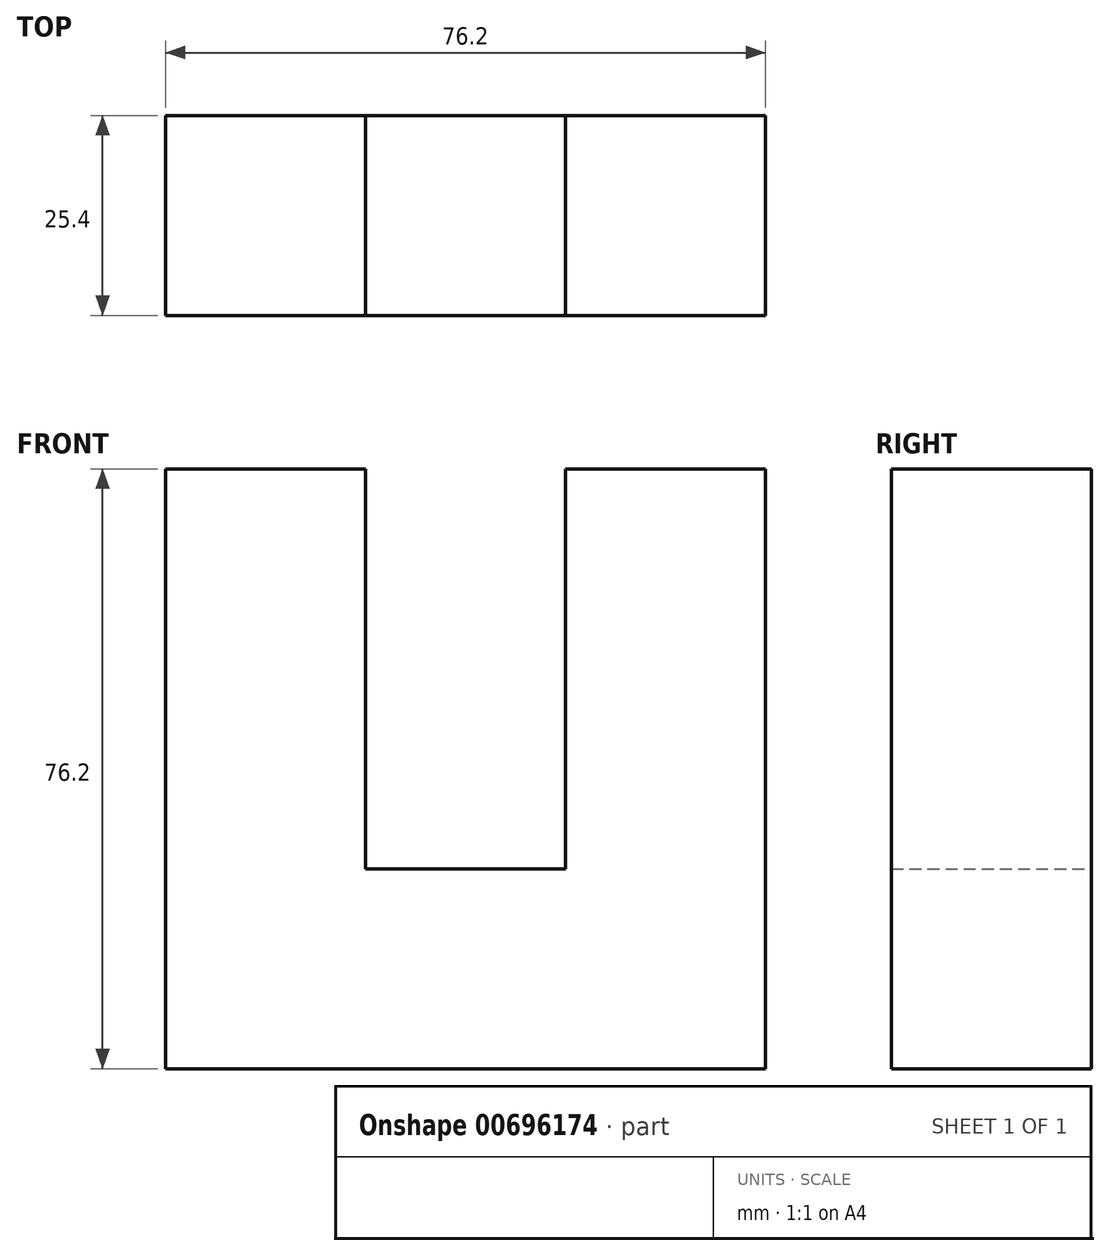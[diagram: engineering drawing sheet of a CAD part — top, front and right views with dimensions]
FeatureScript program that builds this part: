
annotation { "Feature Type Name" : "Feature", "Feature Type Description" : "" }
export const myFeature = defineFeature(function(context is Context, id is Id, definition is map)
    precondition{}
    {
        {
            var Q0;
            Q0=qCreatedBy(makeId("Front.planeOp"),FACE);
            var sketch = newSketch(context, id + "F0", { "sketchPlane" : qUnion([Q0])});
            skLineSegment(sketch, "E0", {"start": v(-25.4, 48.41) * mm, "end": v(-25.4, -27.79) * mm});
            skLineSegment(sketch, "E1", {"start": v(-25.4, -27.79) * mm, "end": v(50.8, -27.79) * mm});
            skLineSegment(sketch, "E2", {"start": v(50.8, -27.79) * mm, "end": v(50.8, 48.41) * mm});
            skLineSegment(sketch, "E3", {"start": v(50.8, 48.41) * mm, "end": v(25.4, 48.41) * mm});
            skLineSegment(sketch, "E4", {"start": v(25.4, 48.41) * mm, "end": v(25.4, -2.39) * mm});
            skLineSegment(sketch, "E5", {"start": v(25.4, -2.39) * mm, "end": v(0, -2.39) * mm});
            skLineSegment(sketch, "E6", {"start": v(0, -2.39) * mm, "end": v(0, 48.41) * mm});
            skLineSegment(sketch, "E7", {"start": v(-25.4, 48.41) * mm, "end": v(0, 48.41) * mm});
            skSolve(sketch);
        }
        {
            var Q0;
            Q0=makeQuery(id+"F0.imprint","IMPRINT",FACE,{"disambiguationData":[TD([[makeQuery(id+"F0.imprint","IMPRINT",EDGE,{"derivedFrom":sQuery(id+"F0.wireOp",EDGE,"E0")}),1.0]])]});
            extrude(context, id + "F1", {"entities" : qUnion([Q0]), "depth" : 25.4 * mm, "offsetDistance" : 25.4 * mm});
        }
    });
